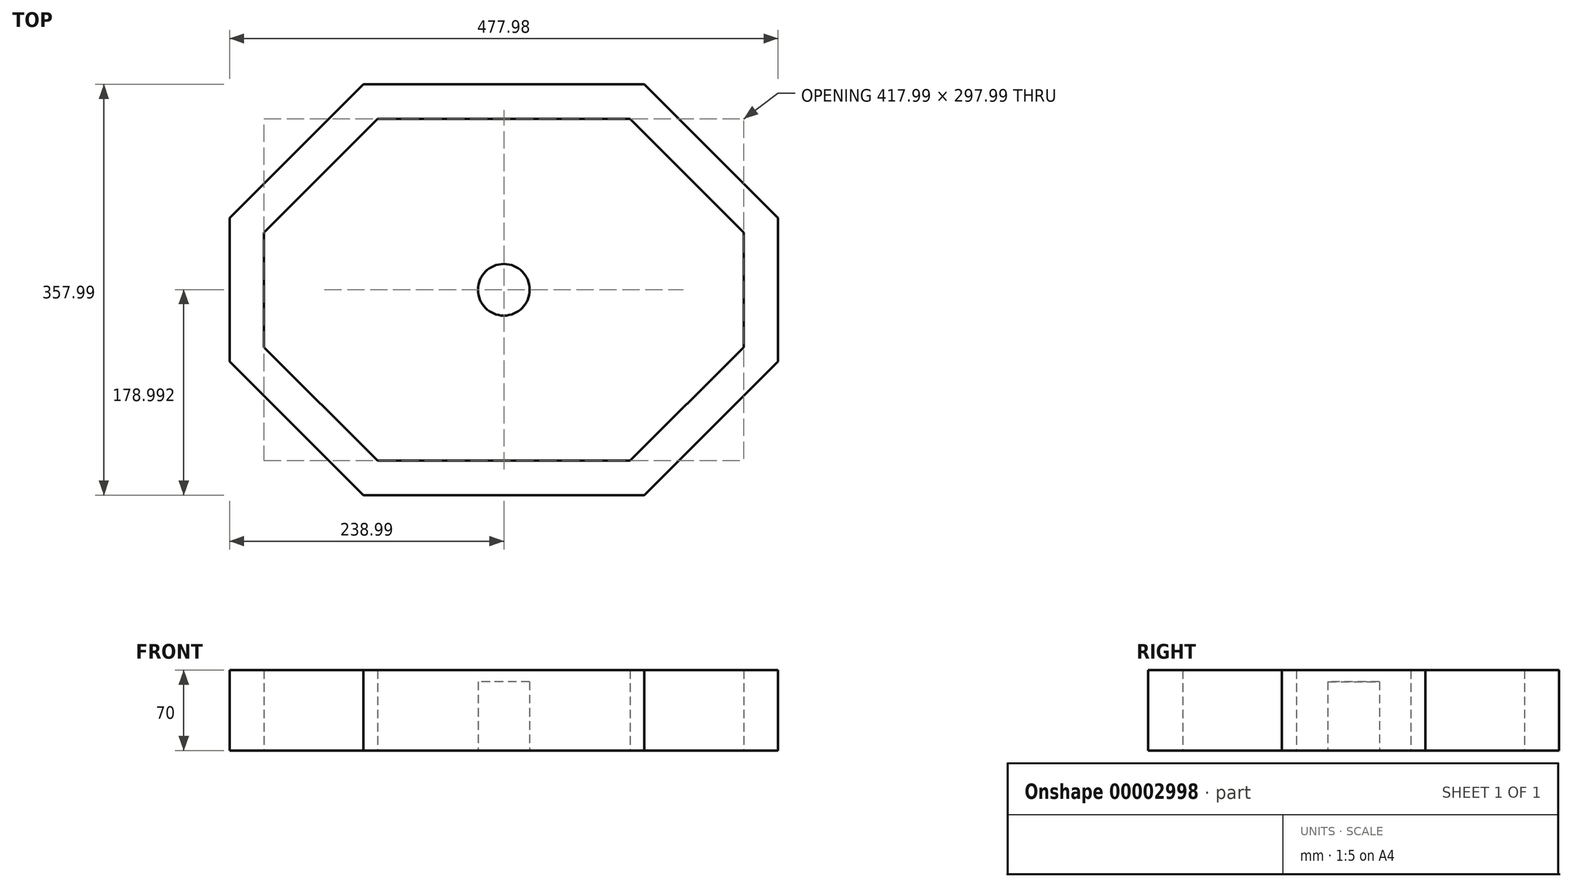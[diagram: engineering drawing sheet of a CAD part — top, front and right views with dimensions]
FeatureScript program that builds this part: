
annotation { "Feature Type Name" : "Feature", "Feature Type Description" : "" }
export const myFeature = defineFeature(function(context is Context, id is Id, definition is map)
    precondition{}
    {
        {
            var Q0;
            Q0=qCreatedBy(makeId("Top.planeOp"),FACE);
            var sketch = newSketch(context, id + "F0", { "sketchPlane" : qUnion([Q0])});
            skLineSegment(sketch, "E0.rect.top", {"start": v(110, -37.26) * mm, "end": v(-110, -37.26) * mm});
            skPoint(sketch, "E0.rect.middle", {"position": v(0, -76.02) * mm});
            skLineSegment(sketch, "E1", {"start": v(-110, -37.26) * mm, "end": v(-209, 61.73) * mm});
            skLineSegment(sketch, "E2", {"start": v(-209, 61.73) * mm, "end": v(-209, 161.73) * mm});
            skLineSegment(sketch, "E3", {"start": v(-209, 161.73) * mm, "end": v(-110, 260.73) * mm});
            skLineSegment(sketch, "E4", {"start": v(-110, 260.73) * mm, "end": v(110, 260.73) * mm});
            skLineSegment(sketch, "E5", {"start": v(110, 260.73) * mm, "end": v(209, 161.73) * mm});
            skLineSegment(sketch, "E6", {"start": v(209, 161.73) * mm, "end": v(209, 61.73) * mm});
            skLineSegment(sketch, "E7", {"start": v(209, 61.73) * mm, "end": v(110, -37.26) * mm});
            skLineSegment(sketch, "E8", {"start": v(-110, 260.73) * mm, "end": v(110, -37.26) * mm, "construction": true});
            skLineSegment(sketch, "E9", {"start": v(-110, -37.26) * mm, "end": v(110, 260.73) * mm, "construction": true});
            skLineSegment(sketch, "E10", {"start": v(209, 61.73) * mm, "end": v(-209, 161.73) * mm, "construction": true});
            skCircle(sketch, "E11", {"center": v(0, 111.73) * mm, "radius": 22.5 * mm});
            skLineSegment(sketch, "E12.0", {"start": v(-239, 174.16) * mm, "end": v(-122.43, 290.73) * mm});
            skLineSegment(sketch, "E12.1", {"start": v(-239, 49.3) * mm, "end": v(-239, 174.16) * mm});
            skLineSegment(sketch, "E12.2", {"start": v(-122.43, -67.26) * mm, "end": v(-239, 49.3) * mm});
            skLineSegment(sketch, "E12.3", {"start": v(122.43, -67.26) * mm, "end": v(-122.43, -67.26) * mm});
            skLineSegment(sketch, "E12.4", {"start": v(239, 49.3) * mm, "end": v(122.43, -67.26) * mm});
            skLineSegment(sketch, "E12.5", {"start": v(-122.43, 290.73) * mm, "end": v(122.43, 290.73) * mm});
            skLineSegment(sketch, "E12.6", {"start": v(239, 174.16) * mm, "end": v(239, 49.3) * mm});
            skLineSegment(sketch, "E12.7", {"start": v(122.43, 290.73) * mm, "end": v(239, 174.16) * mm});
            skLineSegment(sketch, "E13", {"start": v(-110, 260.73) * mm, "end": v(-110, -37.26) * mm, "construction": true});
            skLineSegment(sketch, "E14", {"start": v(110, -37.26) * mm, "end": v(110, 260.73) * mm, "construction": true});
            skLineSegment(sketch, "E15", {"start": v(-209, 161.73) * mm, "end": v(209, 161.73) * mm, "construction": true});
            skLineSegment(sketch, "E16", {"start": v(209, 61.73) * mm, "end": v(-209, 61.73) * mm, "construction": true});
            skLineSegment(sketch, "E17", {"start": v(-209, 61.73) * mm, "end": v(-36.91, 61.73) * mm});
            skLineSegment(sketch, "E18", {"start": v(-110, 61.73) * mm, "end": v(-110, -37.26) * mm});
            skSolve(sketch);
        }
        {
            var Q0;
            Q0=makeQuery(id+"F0.imprint","IMPRINT",FACE,{"disambiguationData":[TD([[makeQuery(id+"F0.imprint","IMPRINT",EDGE,{"derivedFrom":sQuery(id+"F0.wireOp",EDGE,"E0.rect.top")}),1.0]])]});
            extrude(context, id + "F1", {"entities" : qUnion([Q0]), "depth" : 70 * mm});
        }
        {
            var Q0;
            Q0=makeQuery(id+"F0.imprint","IMPRINT",FACE,{"disambiguationData":[TD([[makeQuery(id+"F0.imprint","IMPRINT",EDGE,{"derivedFrom":sQuery(id+"F0.wireOp",EDGE,"E11")}),1.0]])]});
            extrude(context, id + "F2", {"entities" : qUnion([Q0]), "depth" : 60 * mm});
        }
    });
